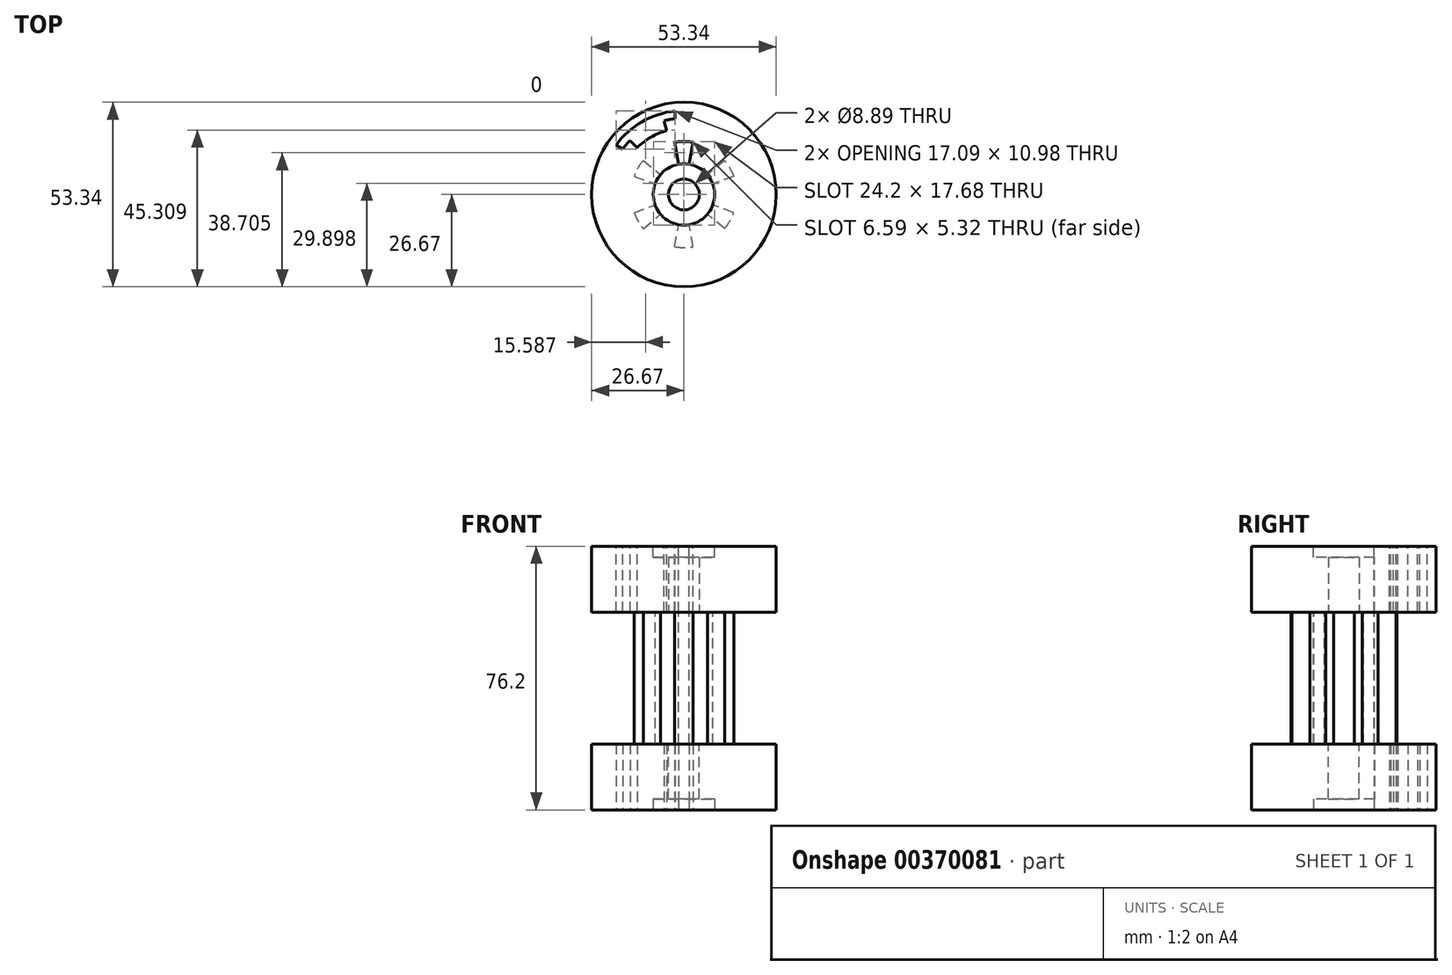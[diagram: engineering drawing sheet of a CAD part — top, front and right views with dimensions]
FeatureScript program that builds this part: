
annotation { "Feature Type Name" : "Feature", "Feature Type Description" : "" }
export const myFeature = defineFeature(function(context is Context, id is Id, definition is map)
    precondition{}
    {
        {
            var Q0;
            Q0=qCreatedBy(makeId("Top.planeOp"),FACE);
            var sketch = newSketch(context, id + "F0", { "sketchPlane" : qUnion([Q0])});
            skCircle(sketch, "E0", {"center": v(0, 0) * mm, "radius": 26.67 * mm});
            skCircle(sketch, "E1", {"center": v(0, 0) * mm, "radius": 4.45 * mm});
            skSolve(sketch);
        }
        {
            var Q0;
            Q0 = qSketchRegion(id + "F0", true);
            extrude(context, id + "F1", {"entities" : qUnion([Q0]), "depth" : 19.05 * mm});
        }
        {
            var Q0;
            Q0=makeQuery(id+"F1.opExtrude","CAP_FACE",FACE,{"disambiguationData":[OSD([sQuery(id+"F0.wireOp",EDGE,"E0"),sQuery(id+"F0.wireOp",EDGE,"E1")])],"isStart":false});
            var sketch = newSketch(context, id + "F2", { "sketchPlane" : qUnion([Q0])});
            skCircle(sketch, "E2", {"center": v(0, 0) * mm, "radius": 24.26 * mm, "construction": true});
            skCircle(sketch, "E3", {"center": v(0, 0) * mm, "radius": 22.05 * mm, "construction": true});
            skCircle(sketch, "E4", {"center": v(0, 0) * mm, "radius": 19.11 * mm, "construction": true});
            skLineSegment(sketch, "E5", {"start": v(0, 0) * mm, "end": v(-23.1, 13.34) * mm, "construction": true});
            skLineSegment(sketch, "E6", {"start": v(-2.54, 24.13) * mm, "end": v(-2.54, 21.9) * mm});
            skLineSegment(sketch, "E7", {"start": v(-19.63, 14.26) * mm, "end": v(-17.7, 13.15) * mm});
            skArc(sketch, "E8", {"start": v(-2.54, 24.13) * mm, "mid": v(-12.13, 21.01) * mm, "end": v(-19.63, 14.26) * mm});
            skLineSegment(sketch, "E9", {"start": v(0, 0) * mm, "end": v(-15.59, 15.59) * mm, "construction": true});
            skLineSegment(sketch, "E10", {"start": v(0, 0) * mm, "end": v(-5.7, 21.3) * mm, "construction": true});
            skLineSegment(sketch, "E11", {"start": v(-15.59, 15.59) * mm, "end": v(-13.51, 13.51) * mm});
            skLineSegment(sketch, "E12", {"start": v(-5.7, 21.3) * mm, "end": v(-4.95, 18.46) * mm});
            skArc(sketch, "E13", {"start": v(-17.7, 13.15) * mm, "mid": v(-16.69, 14.4) * mm, "end": v(-15.59, 15.59) * mm});
            skArc(sketch, "E14", {"start": v(-2.54, 21.9) * mm, "mid": v(-4.13, 21.65) * mm, "end": v(-5.7, 21.3) * mm});
            skArc(sketch, "E15", {"start": v(-13.51, 13.51) * mm, "mid": v(-9.56, 16.55) * mm, "end": v(-4.95, 18.46) * mm});
            skSolve(sketch);
        }
        {
            var Q0;
            Q0 = qSketchRegion(id + "F2", true);
            extrude(context, id + "F3", {"entities" : qUnion([Q0]), "operationType" : NewBodyOperationType.REMOVE, "endBound" : BoundingType.THROUGH_ALL, "oppositeDirection" : true, "depth" : 25.4 * mm});
        }
        {
            var Q0;
            Q0=qCreatedBy(makeId("Right.planeOp"),FACE);
            var sketch = newSketch(context, id + "F4", { "sketchPlane" : qUnion([Q0])});
            skLineSegment(sketch, "E16", {"start": v(0, 63.62) * mm, "end": v(0, 1.5) * mm});
            skSolve(sketch);
        }
        {
            var Q0;
            Q0=makeQuery(id+"F1.opExtrude","CAP_FACE",FACE,{"disambiguationData":[OSD([sQuery(id+"F0.wireOp",EDGE,"E0"),sQuery(id+"F0.wireOp",EDGE,"E1")])],"isStart":false});
            var sketch = newSketch(context, id + "F5", { "sketchPlane" : qUnion([Q0])});
            skCircle(sketch, "E17", {"center": v(0, 0) * mm, "radius": 15.33 * mm, "construction": true});
            skCircle(sketch, "E18", {"center": v(0, 0) * mm, "radius": 8.87 * mm, "construction": true});
            skLineSegment(sketch, "E19", {"start": v(0, 0) * mm, "end": v(-2.66, 15.1) * mm, "construction": true});
            skLineSegment(sketch, "E20", {"start": v(0, 0) * mm, "end": v(2.66, 15.1) * mm, "construction": true});
            skLineSegment(sketch, "E21", {"start": v(-2.66, 15.1) * mm, "end": v(-1.54, 8.74) * mm});
            skLineSegment(sketch, "E22", {"start": v(2.66, 15.1) * mm, "end": v(1.54, 8.74) * mm});
            skArc(sketch, "E23", {"start": v(-1.54, 8.74) * mm, "mid": v(0, 8.87) * mm, "end": v(1.54, 8.74) * mm});
            skArc(sketch, "E24", {"start": v(-2.66, 15.1) * mm, "mid": v(0, 15.33) * mm, "end": v(2.66, 15.1) * mm});
            skSolve(sketch);
        }
        {
            var Q0;
            Q0 = qSketchRegion(id + "F5", true);
            extrude(context, id + "F6", {"entities" : qUnion([Q0]), "operationType" : NewBodyOperationType.REMOVE, "endBound" : BoundingType.THROUGH_ALL, "oppositeDirection" : true, "depth" : 25.4 * mm});
        }
        {
            var Q0;
            Q0=makeQuery(id+"F1.opExtrude","CAP_FACE",FACE,{"disambiguationData":[OSD([sQuery(id+"F0.wireOp",EDGE,"E0"),sQuery(id+"F0.wireOp",EDGE,"E1")])],"isStart":false});
            var sketch = newSketch(context, id + "F7", { "sketchPlane" : qUnion([Q0])});
            skCircle(sketch, "E25", {"center": v(0, 0) * mm, "radius": 8.87 * mm});
            skSolve(sketch);
        }
        {
            var Q0;
            Q0 = qSketchRegion(id + "F7", true);
            extrude(context, id + "F8", {"entities" : qUnion([Q0]), "operationType" : NewBodyOperationType.REMOVE, "oppositeDirection" : true, "depth" : 3.17 * mm});
        }
        {
            var Q0;
            Q0=makeQuery(id+"F1.opExtrude","CAP_FACE",FACE,{"disambiguationData":[OSD([sQuery(id+"F0.wireOp",EDGE,"E0"),sQuery(id+"F0.wireOp",EDGE,"E1")])],"isStart":true});
            var sketch = newSketch(context, id + "F9", { "sketchPlane" : qUnion([Q0])});
            skArc(sketch, "E26", {"start": v(-2.66, -15.1) * mm, "mid": v(0, -15.33) * mm, "end": v(2.66, -15.1) * mm});
            skArc(sketch, "E27", {"start": v(-1.54, -8.74) * mm, "mid": v(0, -8.87) * mm, "end": v(1.54, -8.74) * mm});
            skLineSegment(sketch, "E28", {"start": v(2.66, -15.1) * mm, "end": v(1.54, -8.74) * mm});
            skLineSegment(sketch, "E29", {"start": v(-2.66, -15.1) * mm, "end": v(-1.54, -8.74) * mm});
            skSolve(sketch);
        }
        {
            var Q0;
            Q0 = qSketchRegion(id + "F9", true);
            extrude(context, id + "F10", {"entities" : qUnion([Q0]), "depth" : 38.1 * mm});
        }
        {
            var Q0;
            Q0=makeQuery(id+"F10.opExtrude","SWEPT_BODY",BODY,{"disambiguationData":[OSD([sQuery(id+"F9.wireOp",EDGE,"E26"),sQuery(id+"F9.wireOp",EDGE,"E27"),sQuery(id+"F9.wireOp",EDGE,"E28"),sQuery(id+"F9.wireOp",EDGE,"E29")])]});
            var Q1;
            Q1=sQuery(id+"F4.wireOp",EDGE,"E16");
            circularPattern(context, id + "F11", {"entities" : qUnion([Q0]), "axis" : qUnion([Q1]), "angle" : 360 * degree, "instanceCount" : 6, "equalSpace" : true});
        }
        {
            var Q0;
            Q0=qCreatedBy(makeId("Top.planeOp"),FACE);
            cPlane(context, id + "F12", {"entities" : qUnion([Q0]), "cplaneType" : CPlaneType.OFFSET, "offset" : 19.05 * mm, "oppositeDirection" : true, "width" : 152.4 * mm, "height" : 152.4 * mm});
        }
        {
            var Q0;
            Q0=makeQuery(id+"F1.opExtrude","SWEPT_BODY",BODY,{"disambiguationData":[OSD([sQuery(id+"F0.wireOp",EDGE,"E0"),sQuery(id+"F0.wireOp",EDGE,"E1")])]});
            var Q1;
            Q1=qCreatedBy(id+"F12.planeOp",FACE);
            mirror(context, id + "F13", {"entities" : qUnion([Q0]), "mirrorPlane" : qUnion([Q1])});
        }
    });
